# Revit family: VITOCAL 200-A PRO AWO-AC 202.A064
name_source: partatom
category: Mechanical Equipment
units: mm (PartAtom-declared; Revit-internal decimal feet)

## family parameters
Always vertical = Yes
Cut with Voids When Loaded = No
OmniClass Number = 23.75.10.21.17
OmniClass Title = Water-Source Heat Pumps
Part Type = Normal
Room Calculation Point = No
Round Connector Dimension = Use Diameter
Shared = No
Work Plane-Based = No

## types (1)
- VITOCAL 200-A PRO AWO-AC 202.A064
    Autor = www.archispace.pl
    Default Elevation = 0 mm  [stored 0 ft]
    Description = Pompa ciepła Vitocal 200-A PRO pozyskuje energię cieplną z powietrza zewnętrznego i wykorzystuje ją do ogrzewania
wody w obiegu grzewczym lub obiegu ciepłej wody użytkowej. Dzięki nagrzewnicy powietrznej (parownik) energia cieplna,
pochodząca ze stale zasysanego przez wentylator powietrza zewnętrznego, jest oddawana do czynnika roboczego
(czynnika chłodniczego). Czynnik chłodniczy ulega przy tym parowaniu. Za pomocą elektrycznie napędzanej sprężarki
zwiększana jest temperatura czynnika chłodniczego w postaci gazowej.
Po odparowaniu i zagęszczeniu energia cieplna z czynnika chłodniczego poprzez kondensację w wymienniku ciepła jest
przekazywana do zasobnika buforowego (nie należy do zakresu dostawy), a następnie do systemu grzewczego. W tzw.
skraplaczu czynnik chłodniczy znów jest skraplany i może zostać ponownie doprowadzony do parownika przez zawór
rozprężny.
Przy niskich temperaturach otoczenia wilgoć odkłada się w parowniku jako szron, co niekorzystnie wpływa
na przekazywanie ciepła. W razie potrzeby parownik jest automatycznie rozmrażany przez pompę ciepła. W zależności
od warunków pogodowych w wylocie powietrza może powstawać para. W zależności od warunków regionalnych konieczna
może być optymalizacja podczas pracy.
Aby zapewnić izolację akustyczną, zasobnik buforowy musi być podłączony za pomocą elastycznych połączeń przewodów.
Zwiększa to jednocześnie żywotność pompy ciepła.
    Dop. ciśnienie robocze po stronie wtórnej = 6 bar
    Długość całkowita = 1330 mm  [stored 4.36352 ft]
    EER w trybie chłodzenia = 4.83
    Informacja = Pomiar całkowitego poziomu mocy akustycznej w oparciu o normę EN ISO 12102/EN ISO 9614.
    Manufacturer = Viessmann Sp. z o.o.
    Masa całkowita (urządzenie podstawowe bez opcjonalnej obudowy) = 790.00 kg
    Moc elektryczna na podgrzew miski olejowej = 2 x 90
    Model = Pompy ciepła powietrze/woda do ustawienia na zewnątrz z napędem elektrycznym do ogrzewania pomieszczeń i podgrzewu ciepłej wody użytkowej w instalacjach grzewczych: - Do 65°C temperatury na zasilaniu, - W zależności od typu z 1, 2 lub 4 sprężarkami, - Z regulatorem pompy ciepła sterowanym pogodowo i graficznym modułem obsługi do montażu na ścianie.
    Obieg chłodniczy. Armatura zabezpieczająca = A1
    Obieg chłodniczy. Czynnik roboczy = R407C
    Obieg chłodniczy. Ekwiwalent CO2 = 31.9
    Obieg chłodniczy. Ilość czynnika chłodniczego = 18.00 kg
    Obieg chłodniczy. Ilość oleju w sprężarce = 2.8
    Obieg chłodniczy. Olej w sprężarce = Idemitsu FV68S
    Obieg chłodniczy. Potencjał tworzenia efektu cieplarnianego (GWP) = 1774
    Obieg chłodniczy. Sprężarka = Scroll
    Pobór mocy elektrycznej = 14.1 kW
    Poziom mocy akustycznej = 69.7 dB(A)
    Pozyskiwanie ciepła. Ilość wody kondensacyjnej przy wilgotności 87% = 30
    Pozyskiwanie ciepła. Maks. Temperatura powietrza na wlocie = 35 °C
    Pozyskiwanie ciepła. Maks. moc elektryczna wentylatora = 4 x 500 W
    Pozyskiwanie ciepła. Min. Temperatura powietrza na wlocie = –20 °C
    Pozyskiwanie ciepła. Znamionowy przepływ objętościowy powietrza = 13 500 m3/h
    Przyłącza. Zasilanie oraz powrót wody grzewczej (gwint zewnętrzny) = G 2
    Sprężarka. Cos φ = 0.76
    Sprężarka. Maks. pobór mocy elektrycznej sprężarki (A2/W35, włącznie z wentylatorem) = 14.6 kW
    Sprężarka. Maks. przekrój elektrycznych przewodów przyłączeniowych = 16 mm2
    Sprężarka. Maks. prąd roboczy = 53 A
    Sprężarka. Napięcie znamionowe = 3/N/PE 400 V/50 Hz
    Sprężarka. Prąd rozruchowy sprężarki = 122.7
    Sprężarka. Zabezp. przyłącza elektrycznego = i 3 x C63A Kombi
    Stopień efektywności ε (COP) = 4
    Stopień ochrony = IPX4
    Szerokość całkowita = 2315 mm  [stored 7.59514 ft]
    URL = https://www.viessmann.pl
    Viessmann Kolor 1 = Viessmann Kolor 1
    Wentylator. Maks. pobór mocy elektrycznej na 1 wentylator = 500 W
    Wentylator. Napięcie znamionowe = 1/N/PE 230 V/50 Hz
    Wentylator. Zabezpieczenie wewnętrzne = B10A
    Woda grzewcza. Maks. temperatura na zasilaniu = 65 °C
    Woda grzewcza. Min. temperatura na powrocie = 20 °C
    Woda grzewcza. Minimalny przepływ objętościowy (1 sprężarka uruchomiona) = 2100 l/h
    Woda grzewcza. Opory przepływu minimalnego przepływu objętościowego = 1.6 kPa
    Woda grzewcza. Opory przepływu znamionowego przepływu objętościowego = 14.7 kPa
    Woda grzewcza. Pojemność = 8.9 l
    Woda grzewcza. Znamionowy przepływ objętościowy = 9690 l/h
    Wysokość całkowita = 1510 mm  [stored 4.95407 ft]
    Zastosowanie niskotemperaturowe (W35). Efektywność energetyczna ηS (%) = 152
    Zastosowanie niskotemperaturowe (W35). Sezonowy stopień efektywności (SCOP) = 3.88
    Zastosowanie niskotemperaturowe (W35). Znamionowa moc grzewcza Prated (kW) = 51
    Zastosowanie średniotemperaturowe (W55). Efektywność energetyczna ηS = 130
    Zastosowanie średniotemperaturowe (W55). Sezonowy stopień efektywności (SCOP) = 3.31
    Zastosowanie średniotemperaturowe (W55). Znamionowa moc grzewcza Prated (kW) = 54
    Znamionowa moc grzewcza = 56.2 kW
    Znamionowa wydajność chłodzenia = 69.9 kW

note: [stored X ft] marks values corroborated as IEEE doubles in the binary element streams (Revit-internal decimal feet)
